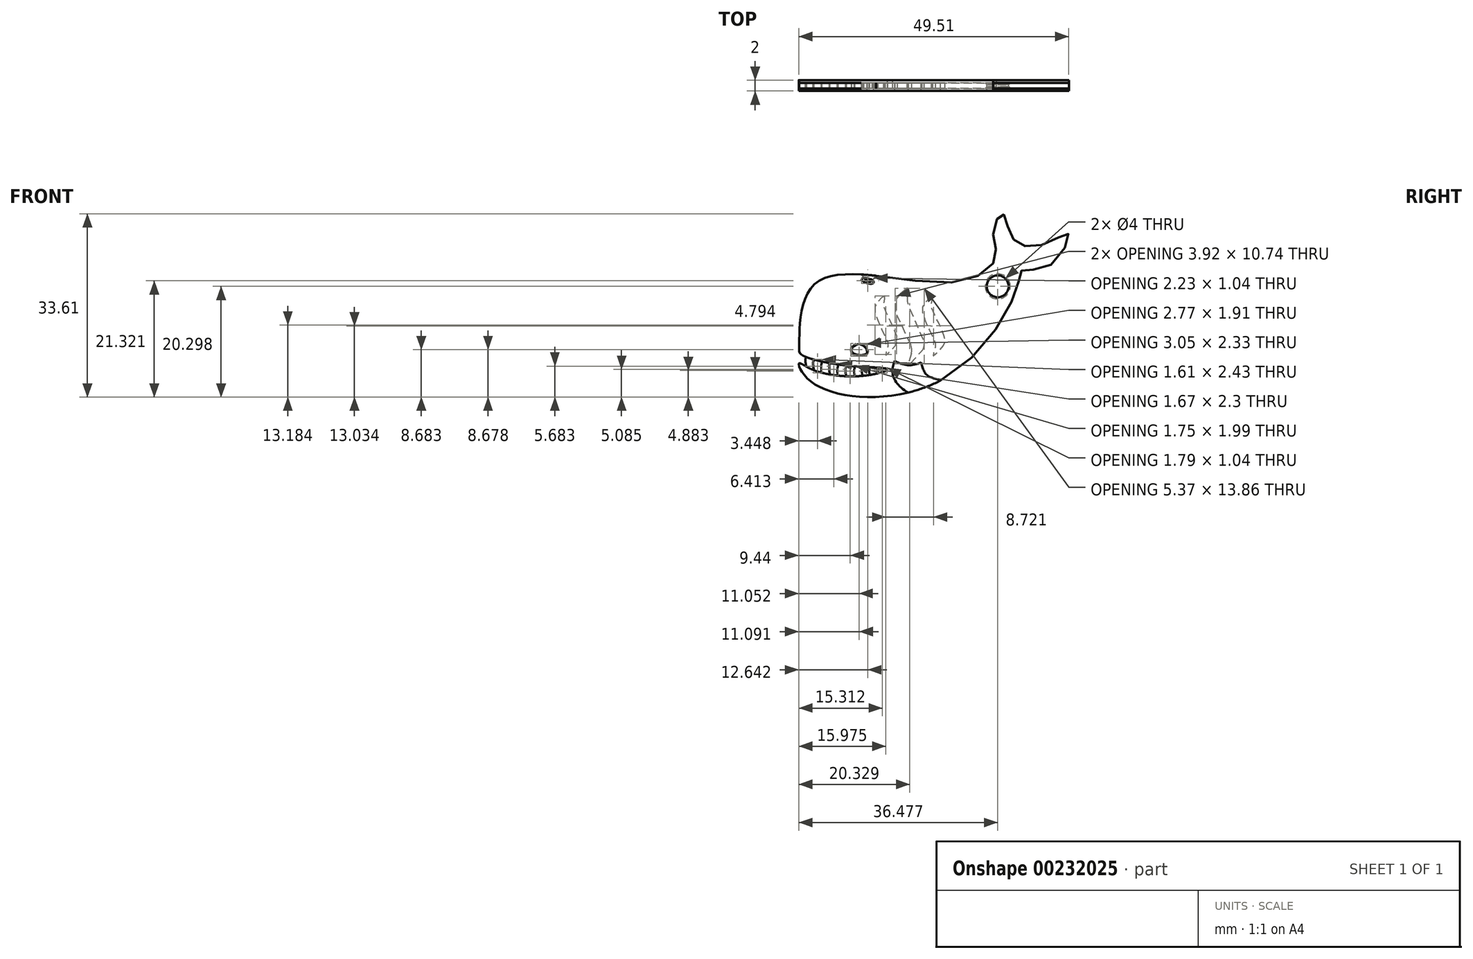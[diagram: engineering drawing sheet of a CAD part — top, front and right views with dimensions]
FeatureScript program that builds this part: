
annotation { "Feature Type Name" : "Feature", "Feature Type Description" : "" }
export const myFeature = defineFeature(function(context is Context, id is Id, definition is map)
    precondition{}
    {
        {
            var Q0;
            Q0=qCreatedBy(makeId("Front.planeOp"),FACE);
            var sketch = newSketch(context, id + "F0", { "sketchPlane" : qUnion([Q0])});
            skFitSpline(sketch, "E0", {"points": [v(-22.86, -10.44) * mm, v(-19.7, 1.07) * mm, v(5.67, 1.15) * mm, v(13.2, 5.95) * mm, v(12.7, 10.48) * mm, v(14.38, 13.69) * mm, v(15.38, 11.35) * mm, v(17.48, 8.08) * mm, v(23.08, 8.54) * mm, v(26.5, 9.96) * mm, v(23.05, 4.16) * mm, v(18, 3.34) * mm, v(17.28, 0.82) * mm, v(3.33, -16.7) * mm, v(-20.33, -17.35) * mm, v(-22.9, -13.75) * mm, v(-20.76, -14.75) * mm, v(-11.12, -16.02) * mm, v(-6.74, -14.84) * mm, v(-13.25, -14.23) * mm, v(-22.52, -12.08) * mm, v(-22.86, -10.44) * mm]});
            skFitSpline(sketch, "E1", {"points": [v(-5.34, -13.25) * mm, v(-5.6, -16.16) * mm, v(-1.36, -19.66) * mm, v(4.85, -18.8) * mm, v(4.28, -17.36) * mm, v(0.7, -15.99) * mm, v(-0.53, -13.57) * mm], "startDerivative": vector(-7.24, -19.66) * mm, "endDerivative": vector(-6.35, 20.95) * mm});
            skArc(sketch, "E2", {"start": v(-22.52, -12.08) * mm, "mid": v(-22.6, -12.94) * mm, "end": v(-22.52, -13.8) * mm});
            skArc(sketch, "E3", {"start": v(-21.63, -12.56) * mm, "mid": v(-21.72, -13.48) * mm, "end": v(-21.48, -14.38) * mm});
            skArc(sketch, "E4", {"start": v(-20.25, -13.02) * mm, "mid": v(-20.3, -14.02) * mm, "end": v(-20.15, -15) * mm});
            skArc(sketch, "E5", {"start": v(-18.7, -13.4) * mm, "mid": v(-18.83, -14.43) * mm, "end": v(-18.73, -15.45) * mm});
            skArc(sketch, "E6", {"start": v(-17.26, -13.69) * mm, "mid": v(-17.37, -14.74) * mm, "end": v(-17.22, -15.78) * mm});
            skArc(sketch, "E7", {"start": v(-15.7, -13.94) * mm, "mid": v(-15.86, -14.96) * mm, "end": v(-15.79, -15.98) * mm});
            skArc(sketch, "E8", {"start": v(-14.18, -14.13) * mm, "mid": v(-14.39, -15.11) * mm, "end": v(-14.2, -16.1) * mm});
            skArc(sketch, "E9", {"start": v(-12.64, -14.28) * mm, "mid": v(-12.77, -15.2) * mm, "end": v(-12.66, -16.11) * mm});
            skArc(sketch, "E10", {"start": v(-11.18, -14.38) * mm, "mid": v(-11.37, -15.2) * mm, "end": v(-11.23, -16.03) * mm});
            skArc(sketch, "E11", {"start": v(-9.9, -14.44) * mm, "mid": v(-10.05, -15.15) * mm, "end": v(-9.9, -15.86) * mm});
            skArc(sketch, "E12", {"start": v(-8.53, -14.52) * mm, "mid": v(-8.52, -15.04) * mm, "end": v(-8.4, -15.56) * mm});
            skFitSpline(sketch, "E13", {"points": [v(-13.24, -11.57) * mm, v(-11.8, -10.24) * mm, v(-10.5, -11.89) * mm, v(-13.24, -11.57) * mm]});
            skEllipse(sketch, "E14", {"center": v(-10.3, 1.4) * mm, "majorRadius": 1.16 * mm, "minorRadius": 0.45 * mm, "majorAxis": v(0.96, -0.26)});
            skFitSpline(sketch, "E15", {"points": [v(-10.43, 1.4) * mm, v(-14.17, 6.8) * mm, v(-14.96, 8.86) * mm, v(-10.3, 6.14) * mm, v(-3.95, 8) * mm, v(-6.2, 5.5) * mm, v(-9.66, 1.4) * mm, v(-10.43, 1.4) * mm]});
            skPoint(sketch, "E16.6.internal.snap0", {"position": v(-2.92, -13.4) * mm});
            skPoint(sketch, "E16.7.internal.snap0", {"position": v(-2.92, -13.4) * mm});
            skArc(sketch, "E17", {"start": v(-5.34, -13.25) * mm, "mid": v(-2.98, -14.05) * mm, "end": v(-0.53, -13.57) * mm});
            skLineSegment(sketch, "E18", {"start": v(-3.11, 0.02) * mm, "end": v(-4.1, -0.8) * mm});
            skLineSegment(sketch, "E19", {"start": v(-5, -4.8) * mm, "end": v(-2.45, -10.33) * mm});
            skLineSegment(sketch, "E20", {"start": v(-2.32, -11.9) * mm, "end": v(-2.79, -13.6) * mm});
            skLineSegment(sketch, "E21", {"start": v(-2.49, -13.76) * mm, "end": v(-0.46, -11.54) * mm});
            skLineSegment(sketch, "E22", {"start": v(-0.1, -9.41) * mm, "end": v(-2.8, -3.16) * mm});
            skLineSegment(sketch, "E23", {"start": v(-3.07, -1.42) * mm, "end": v(-2.92, -0.08) * mm});
            skPoint(sketch, "E24", {"position": v(-2.98, -14.05) * mm});
            skPoint(sketch, "E25.visualSharp", {"position": v(-2.98, -14.3) * mm});
            skArc(sketch, "E25.filletArc", {"start": v(-2.79, -13.6) * mm, "mid": v(-2.7, -13.8) * mm, "end": v(-2.49, -13.76) * mm});
            skPoint(sketch, "E26.visualSharp", {"position": v(0.41, -10.6) * mm});
            skArc(sketch, "E26.filletArc", {"start": v(-0.46, -11.54) * mm, "mid": v(0.04, -10.53) * mm, "end": v(-0.1, -9.41) * mm});
            skPoint(sketch, "E27.visualSharp", {"position": v(-2.1, -11.1) * mm});
            skArc(sketch, "E27.filletArc", {"start": v(-2.32, -11.9) * mm, "mid": v(-2.25, -11.1) * mm, "end": v(-2.45, -10.33) * mm});
            skArc(sketch, "E28.filletArc", {"start": v(-4.1, -0.8) * mm, "mid": v(-5.23, -2.64) * mm, "end": v(-5, -4.8) * mm});
            skPoint(sketch, "E29.visualSharp", {"position": v(-3.17, -2.33) * mm});
            skArc(sketch, "E29.filletArc", {"start": v(-3.07, -1.42) * mm, "mid": v(-3.05, -2.31) * mm, "end": v(-2.8, -3.16) * mm});
            skPoint(sketch, "E30.visualSharp", {"position": v(-2.9, 0.2) * mm});
            skArc(sketch, "E30.filletArc", {"start": v(-2.92, -0.08) * mm, "mid": v(-2.98, 0.03) * mm, "end": v(-3.11, 0.02) * mm});
            skFitSpline(sketch, "E31", {"points": [v(1.52, -1.5) * mm, v(0.32, -2.5) * mm, v(-0.29, -4.28) * mm, v(1.9, -9.56) * mm, v(2.06, -10.88) * mm, v(1.68, -12.33) * mm, v(2.58, -11.58) * mm, v(3.74, -10.17) * mm, v(3.57, -8.31) * mm, v(1.55, -3.91) * mm, v(1.42, -2.58) * mm, v(1.52, -1.5) * mm]});
            skFitSpline(sketch, "E32", {"points": [v(-7.2, -1.37) * mm, v(-8.4, -2.38) * mm, v(-9, -4.15) * mm, v(-6.82, -9.43) * mm, v(-6.66, -10.75) * mm, v(-7.04, -12.2) * mm, v(-6.14, -11.45) * mm, v(-4.98, -10.04) * mm, v(-5.15, -8.18) * mm, v(-7.17, -3.78) * mm, v(-7.3, -2.44) * mm, v(-7.2, -1.37) * mm]});
            skFitSpline(sketch, "E33.0", {"points": [v(-8.94, 0.9) * mm, v(-8.89, 1.01) * mm, v(-8.87, 1.14) * mm, v(-8.89, 1.3) * mm, v(-8.96, 1.45) * mm, v(-9.09, 1.6) * mm, v(-9.25, 1.74) * mm, v(-9.43, 1.86) * mm, v(-9.7, 2) * mm, v(-10.1, 2.15) * mm, v(-10.52, 2.23) * mm, v(-10.83, 2.24) * mm, v(-11.05, 2.24) * mm, v(-11.25, 2.2) * mm, v(-11.44, 2.13) * mm, v(-11.59, 2.03) * mm, v(-11.68, 1.9) * mm, v(-11.73, 1.79) * mm, v(-11.74, 1.67) * mm, v(-11.73, 1.5) * mm, v(-11.65, 1.35) * mm, v(-11.53, 1.2) * mm, v(-11.37, 1.06) * mm, v(-11.18, 0.94) * mm, v(-10.9, 0.8) * mm, v(-10.51, 0.65) * mm, v(-10.1, 0.58) * mm, v(-9.79, 0.56) * mm, v(-9.57, 0.57) * mm, v(-9.36, 0.6) * mm, v(-9.17, 0.67) * mm, v(-9.03, 0.77) * mm, v(-8.94, 0.9) * mm, v(-8.89, 1.01) * mm, v(-8.87, 1.14) * mm, v(-8.94, 0.9) * mm]});
            skCircle(sketch, "E34", {"center": v(13.53, 0.38) * mm, "radius": 2 * mm});
            skSolve(sketch);
        }
        {
            var Q0;
            Q0=makeQuery(id+"F0.imprint","IMPRINT",FACE,{"disambiguationData":[TD([[makeQuery(id+"F0.imprint","IMPRINT",EDGE,{"derivedFrom":sQuery(id+"F0.wireOp",EDGE,"E13")}),1.0]])]});
            var Q1;
            {var subQ0=sQuery(id+"F0.wireOp",EDGE,"E15");var subQ1=sQuery(id+"F0.wireOp",EDGE,"E14");var subQ2=makeQuery(id+"F0.imprint","INTERSECT",VERTEX,{"disambiguationData":[OD(0.0)],"derivedFrom":[subQ1,subQ0]});Q1=makeQuery(id+"F0.imprint","IMPRINT",FACE,{"disambiguationData":[TD([[makeQuery(id+"F0.imprint","IMPRINT",EDGE,{"disambiguationData":[TD([[subQ2,1.0]])],"derivedFrom":subQ1}),1.0]])]});}
            var Q2;
            {var subQ0=sQuery(id+"F0.wireOp",EDGE,"E3");Q2=makeQuery(id+"F0.imprint","IMPRINT",FACE,{"disambiguationData":[TD([[makeQuery(id+"F0.imprint","IMPRINT",EDGE,{"derivedFrom":subQ0}),1.0]])]});}
            var Q3;
            {var subQ0=sQuery(id+"F0.wireOp",EDGE,"E5");Q3=makeQuery(id+"F0.imprint","IMPRINT",FACE,{"disambiguationData":[TD([[makeQuery(id+"F0.imprint","IMPRINT",EDGE,{"derivedFrom":subQ0}),1.0]])]});}
            var Q4;
            {var subQ0=sQuery(id+"F0.wireOp",EDGE,"E7");Q4=makeQuery(id+"F0.imprint","IMPRINT",FACE,{"disambiguationData":[TD([[makeQuery(id+"F0.imprint","IMPRINT",EDGE,{"derivedFrom":subQ0}),1.0]])]});}
            var Q5;
            {var subQ0=sQuery(id+"F0.wireOp",EDGE,"E9");Q5=makeQuery(id+"F0.imprint","IMPRINT",FACE,{"disambiguationData":[TD([[makeQuery(id+"F0.imprint","IMPRINT",EDGE,{"derivedFrom":subQ0}),1.0]])]});}
            var Q6;
            {var subQ0=sQuery(id+"F0.wireOp",EDGE,"E11");Q6=makeQuery(id+"F0.imprint","IMPRINT",FACE,{"disambiguationData":[TD([[makeQuery(id+"F0.imprint","IMPRINT",EDGE,{"derivedFrom":subQ0}),1.0]])]});}
            var Q7;
            {var subQ0=sQuery(id+"F0.wireOp",EDGE,"E17");Q7=makeQuery(id+"F0.imprint","IMPRINT",FACE,{"disambiguationData":[TD([[makeQuery(id+"F0.imprint","IMPRINT",EDGE,{"derivedFrom":subQ0}),-1.0]])]});}
            var Q8;
            {var subQ0=sQuery(id+"F0.wireOp",EDGE,"E15");var subQ1=sQuery(id+"F0.wireOp",EDGE,"E0");var subQ2=makeQuery(id+"F0.imprint","INTERSECT",VERTEX,{"disambiguationData":[OD(0.0)],"derivedFrom":[subQ1,subQ0]});Q8=makeQuery(id+"F0.imprint","IMPRINT",FACE,{"disambiguationData":[TD([[makeQuery(id+"F0.imprint","IMPRINT",EDGE,{"disambiguationData":[TD([[subQ2,-1.0]])],"derivedFrom":subQ1}),1.0]])]});}
            var Q9;
            {var subQ0=sQuery(id+"F0.wireOp",EDGE,"E15");var subQ1=sQuery(id+"F0.wireOp",EDGE,"E0");var subQ2=makeQuery(id+"F0.imprint","INTERSECT",VERTEX,{"disambiguationData":[OD(0.0)],"derivedFrom":[subQ1,subQ0]});Q9=makeQuery(id+"F0.imprint","IMPRINT",FACE,{"disambiguationData":[TD([[makeQuery(id+"F0.imprint","IMPRINT",EDGE,{"disambiguationData":[TD([[subQ2,-1.0]])],"derivedFrom":subQ1}),-1.0]])]});}
            extrude(context, id + "F1", {"entities" : qUnion([Q0, Q1, Q2, Q3, Q4, Q5, Q6, Q7, Q8, Q9]), "endBound" : BoundingType.SYMMETRIC, "depth" : 1 * mm});
        }
        {
            var Q0;
            Q0=makeQuery(id+"F0.imprint","IMPRINT",FACE,{"disambiguationData":[TD([[makeQuery(id+"F0.imprint","IMPRINT",EDGE,{"derivedFrom":sQuery(id+"F0.wireOp",EDGE,"E32")}),1.0]])]});
            var Q1;
            Q1=makeQuery(id+"F0.imprint","IMPRINT",FACE,{"disambiguationData":[TD([[makeQuery(id+"F0.imprint","IMPRINT",EDGE,{"derivedFrom":sQuery(id+"F0.wireOp",EDGE,"E18")}),1.0]])]});
            var Q2;
            Q2=makeQuery(id+"F0.imprint","IMPRINT",FACE,{"disambiguationData":[TD([[makeQuery(id+"F0.imprint","IMPRINT",EDGE,{"derivedFrom":sQuery(id+"F0.wireOp",EDGE,"E31")}),1.0]])]});
            var Q3;
            {var subQ0=sQuery(id+"F0.wireOp",EDGE,"E15");var subQ1=sQuery(id+"F0.wireOp",EDGE,"E14");var subQ2=makeQuery(id+"F0.imprint","INTERSECT",VERTEX,{"disambiguationData":[OD(0.0)],"derivedFrom":[subQ1,subQ0]});Q3=makeQuery(id+"F0.imprint","IMPRINT",FACE,{"disambiguationData":[TD([[makeQuery(id+"F0.imprint","IMPRINT",EDGE,{"disambiguationData":[TD([[subQ2,-1.0]])],"derivedFrom":subQ1}),-1.0]])]});}
            var Q4;
            {var subQ0=sQuery(id+"F0.wireOp",EDGE,"E15");var subQ1=sQuery(id+"F0.wireOp",EDGE,"E14");var subQ2=makeQuery(id+"F0.imprint","INTERSECT",VERTEX,{"disambiguationData":[OD(0.0)],"derivedFrom":[subQ1,subQ0]});Q4=makeQuery(id+"F0.imprint","IMPRINT",FACE,{"disambiguationData":[TD([[makeQuery(id+"F0.imprint","IMPRINT",EDGE,{"disambiguationData":[TD([[subQ2,1.0]])],"derivedFrom":subQ1}),-1.0]])]});}
            extrude(context, id + "F2", {"entities" : qUnion([Q0, Q1, Q2, Q3, Q4]), "endBound" : BoundingType.SYMMETRIC, "depth" : 2 * mm});
        }
        {
            var Q0;
            Q0=makeQuery(id+"F1.opExtrude","CAP_EDGE",EDGE,{"disambiguationData":[OSD([sQuery(id+"F0.wireOp",EDGE,"E13")])],"isStart":false});
            var Q1;
            Q1=makeQuery(id+"F1.opExtrude","CAP_EDGE",EDGE,{"disambiguationData":[OSD([sQuery(id+"F0.wireOp",EDGE,"E13")])],"isStart":true});
            fillet(context, id + "F3", {"entities" : qUnion([Q0, Q1]), "radius" : .2 * mm, "tangentPropagation" : true, "allowEdgeOverflow" : false});
        }
        {
            var Q0;
            Q0=makeQuery(id+"F1.opExtrude","CAP_EDGE",EDGE,{"disambiguationData":[OSD([sQuery(id+"F0.wireOp",EDGE,"E34")])],"isStart":false});
            var Q1;
            Q1=makeQuery(id+"F1.opExtrude","CAP_EDGE",EDGE,{"disambiguationData":[OSD([sQuery(id+"F0.wireOp",EDGE,"E34")])],"isStart":true});
            chamfer(context, id + "F4", {"entities" : qUnion([Q0, Q1]), "width" : .3 * mm, "tangentPropagation" : true});
        }
    });
